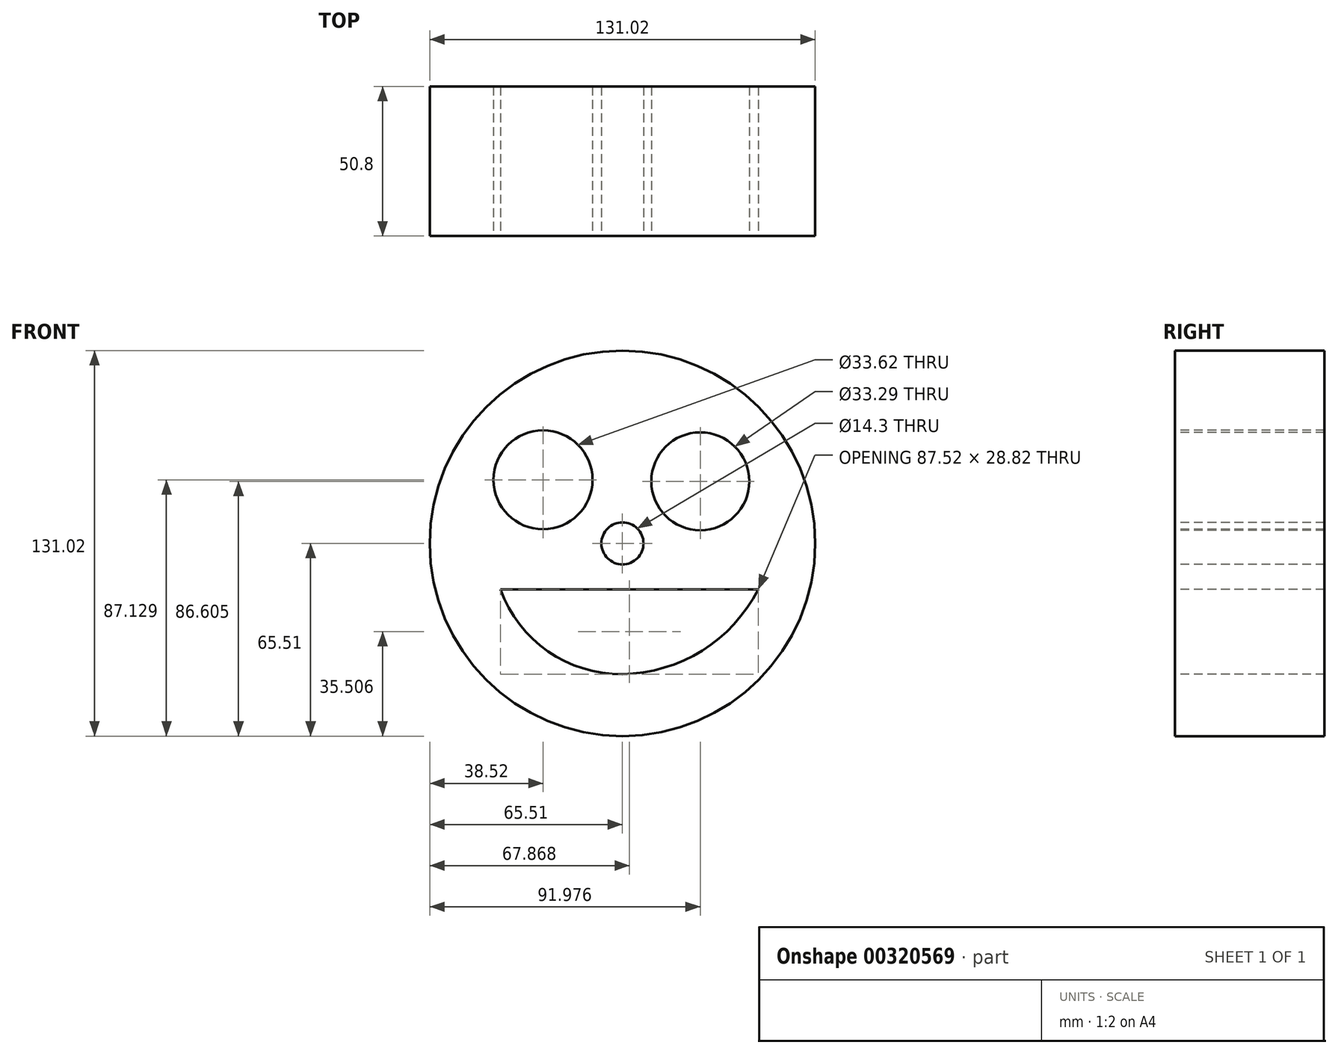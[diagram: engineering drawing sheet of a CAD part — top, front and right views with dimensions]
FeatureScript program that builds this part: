
annotation { "Feature Type Name" : "Feature", "Feature Type Description" : "" }
export const myFeature = defineFeature(function(context is Context, id is Id, definition is map)
    precondition{}
    {
        {
            var Q0;
            Q0=qCreatedBy(makeId("Front.planeOp"),FACE);
            var sketch = newSketch(context, id + "F0", { "sketchPlane" : qUnion([Q0])});
            skCircle(sketch, "E0", {"center": v(0, 0) * mm, "radius": 65.51 * mm});
            skArc(sketch, "E1", {"start": v(-41.4, -15.6) * mm, "mid": v(-25.34, -36.66) * mm, "end": v(0, -44.42) * mm});
            skArc(sketch, "E2", {"start": v(0, -44.42) * mm, "mid": v(27.08, -36.44) * mm, "end": v(46.12, -15.6) * mm});
            skLineSegment(sketch, "E3", {"start": v(-41.4, -15.6) * mm, "end": v(46.12, -15.6) * mm});
            skCircle(sketch, "E4", {"center": v(-27, 21.62) * mm, "radius": 16.8 * mm});
            skCircle(sketch, "E5", {"center": v(26.47, 21.1) * mm, "radius": 16.65 * mm});
            skPoint(sketch, "E6.start.orphan", {"position": v(0, 30) * mm});
            skCircle(sketch, "E7", {"center": v(0, 0) * mm, "radius": 7.15 * mm});
            skSolve(sketch);
        }
        {
            var Q0;
            Q0 = qSketchRegion(id + "F0", true);
            extrude(context, id + "F1", {"entities" : qUnion([Q0]), "oppositeDirection" : true, "depth" : 50.8 * mm});
        }
    });
